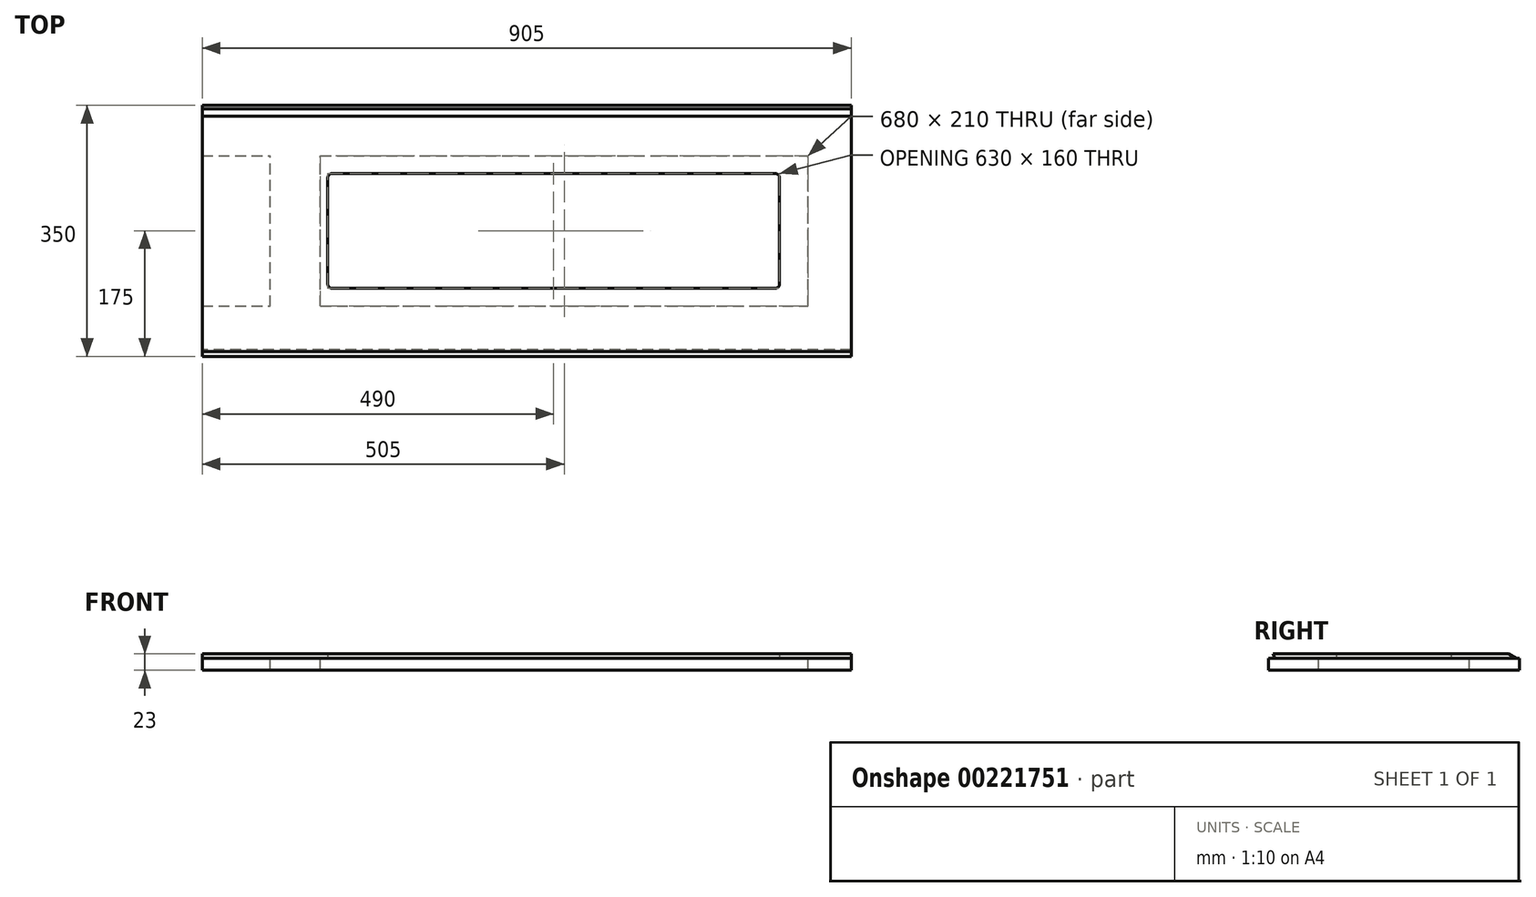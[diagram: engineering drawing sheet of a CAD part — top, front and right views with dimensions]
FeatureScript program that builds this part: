
annotation { "Feature Type Name" : "Feature", "Feature Type Description" : "" }
export const myFeature = defineFeature(function(context is Context, id is Id, definition is map)
    precondition{}
    {
        {
            var Q0;
            Q0=qCreatedBy(makeId("Top.planeOp"),FACE);
            var sketch = newSketch(context, id + "F0", { "sketchPlane" : qUnion([Q0])});
            skLineSegment(sketch, "E0.bottom", {"start": v(-452.5, 175) * mm, "end": v(452.5, 175) * mm});
            skLineSegment(sketch, "E0.top", {"start": v(-452.5, -175) * mm, "end": v(452.5, -175) * mm});
            skLineSegment(sketch, "E0.left", {"start": v(-452.5, 175) * mm, "end": v(-452.5, -175) * mm});
            skLineSegment(sketch, "E0.right", {"start": v(452.5, 175) * mm, "end": v(452.5, -175) * mm});
            skPoint(sketch, "E0.middle", {"position": v(0, 0) * mm});
            skLineSegment(sketch, "E1.bottom", {"start": v(-271.5, 80) * mm, "end": v(346.5, 80) * mm});
            skLineSegment(sketch, "E1.top", {"start": v(-271.5, -80) * mm, "end": v(346.5, -80) * mm});
            skLineSegment(sketch, "E1.left", {"start": v(-277.5, 74) * mm, "end": v(-277.5, -74) * mm});
            skLineSegment(sketch, "E1.right", {"start": v(352.5, 74) * mm, "end": v(352.5, -74) * mm});
            skPoint(sketch, "E2.visualSharp", {"position": v(-277.5, -80) * mm});
            skArc(sketch, "E2.filletArc", {"start": v(-277.5, -74) * mm, "mid": v(-275.74, -78.24) * mm, "end": v(-271.5, -80) * mm});
            skPoint(sketch, "E3.visualSharp", {"position": v(352.5, -80) * mm});
            skArc(sketch, "E3.filletArc", {"start": v(346.5, -80) * mm, "mid": v(350.74, -78.24) * mm, "end": v(352.5, -74) * mm});
            skPoint(sketch, "E4.visualSharp", {"position": v(352.5, 80) * mm});
            skArc(sketch, "E4.filletArc", {"start": v(352.5, 74) * mm, "mid": v(350.74, 78.24) * mm, "end": v(346.5, 80) * mm});
            skLineSegment(sketch, "E5", {"start": v(0, 0) * mm, "end": v(163.88, 0) * mm, "construction": true});
            skLineSegment(sketch, "E6", {"start": v(0, 0) * mm, "end": v(0, -200.2) * mm, "construction": true});
            skPoint(sketch, "E7.visualSharp", {"position": v(-277.5, 80) * mm});
            skArc(sketch, "E7.filletArc", {"start": v(-271.5, 80) * mm, "mid": v(-275.74, 78.24) * mm, "end": v(-277.5, 74) * mm});
            skSolve(sketch);
        }
        {
            var Q0;
            Q0 = qSketchRegion(id + "F0", true);
            extrude(context, id + "F1", {"entities" : qUnion([Q0]), "depth" : 6 * mm});
        }
        {
            var Q0;
            Q0=makeQuery(id+"F1.opExtrude","CAP_FACE",FACE,{"disambiguationData":[OSD([sQuery(id+"F0.wireOp",EDGE,"E0.bottom"),sQuery(id+"F0.wireOp",EDGE,"E0.top"),sQuery(id+"F0.wireOp",EDGE,"E0.left"),sQuery(id+"F0.wireOp",EDGE,"E0.right"),sQuery(id+"F0.wireOp",EDGE,"E1.bottom"),sQuery(id+"F0.wireOp",EDGE,"E1.top"),sQuery(id+"F0.wireOp",EDGE,"E1.left"),sQuery(id+"F0.wireOp",EDGE,"E1.right"),sQuery(id+"F0.wireOp",EDGE,"E2.filletArc"),sQuery(id+"F0.wireOp",EDGE,"E3.filletArc"),sQuery(id+"F0.wireOp",EDGE,"E4.filletArc"),sQuery(id+"F0.wireOp",EDGE,"E7.filletArc")])],"isStart":true});
            var sketch = newSketch(context, id + "F2", { "sketchPlane" : qUnion([Q0])});
            skLineSegment(sketch, "E8.0", {"start": v(-452.5, 175) * mm, "end": v(452.5, 175) * mm});
            skLineSegment(sketch, "E9.0", {"start": v(-452.5, -175) * mm, "end": v(452.5, -175) * mm});
            skLineSegment(sketch, "E10.0", {"start": v(452.5, -175) * mm, "end": v(452.5, 175) * mm});
            skLineSegment(sketch, "E11", {"start": v(-452.5, 105) * mm, "end": v(452.5, 105) * mm});
            skLineSegment(sketch, "E12.0", {"start": v(-452.5, -175) * mm, "end": v(-452.5, 175) * mm});
            skLineSegment(sketch, "E13", {"start": v(-452.5, -105) * mm, "end": v(452.5, -105) * mm});
            skLineSegment(sketch, "E14", {"start": v(392.5, 105) * mm, "end": v(392.5, -105) * mm});
            skLineSegment(sketch, "E15", {"start": v(-287.5, 105) * mm, "end": v(-287.5, -105) * mm});
            skLineSegment(sketch, "E16", {"start": v(-357.5, 105) * mm, "end": v(-357.5, -105) * mm});
            skSolve(sketch);
        }
        {
            var Q0;
            {var subQ5=sQuery(id+"F2.wireOp",EDGE,"E14");Q0=makeQuery(id+"F2.imprint","IMPRINT",FACE,{"disambiguationData":[TD([[makeQuery(id+"F2.imprint","IMPRINT",EDGE,{"derivedFrom":subQ5}),1.0]])]});}
            var Q1;
            {var subQ5=sQuery(id+"F2.wireOp",EDGE,"E8.0");Q1=makeQuery(id+"F2.imprint","IMPRINT",FACE,{"disambiguationData":[TD([[makeQuery(id+"F2.imprint","IMPRINT",EDGE,{"derivedFrom":subQ5}),-1.0]])]});}
            var Q2;
            {var subQ4=sQuery(id+"F2.wireOp",EDGE,"E9.0");Q2=makeQuery(id+"F2.imprint","IMPRINT",FACE,{"disambiguationData":[TD([[makeQuery(id+"F2.imprint","IMPRINT",EDGE,{"derivedFrom":subQ4}),1.0]])]});}
            var Q3;
            {var subQ0=sQuery(id+"F2.wireOp",EDGE,"E15");Q3=makeQuery(id+"F2.imprint","IMPRINT",FACE,{"disambiguationData":[TD([[makeQuery(id+"F2.imprint","IMPRINT",EDGE,{"derivedFrom":subQ0}),-1.0]])]});}
            extrude(context, id + "F3", {"entities" : qUnion([Q0, Q1, Q2, Q3]), "depth" : 17 * mm});
        }
        {
            var Q0;
            Q0=makeQuery(id+"F1.opExtrude","CAP_EDGE",EDGE,{"disambiguationData":[OSD([sQuery(id+"F0.wireOp",EDGE,"E0.bottom")])],"isStart":false});
            chamfer(context, id + "F4", {"entities" : qUnion([Q0]), "chamferType" : ChamferType.OFFSET_ANGLE, "width" : 15 * mm, "oppositeDirection" : true, "angle" : 30 * degree, "tangentPropagation" : true});
        }
        {
            var Q0;
            Q0=makeQuery(id+"F1.opExtrude","CAP_EDGE",EDGE,{"disambiguationData":[OSD([sQuery(id+"F0.wireOp",EDGE,"E0.top")])],"isStart":true});
            chamfer(context, id + "F5", {"entities" : qUnion([Q0]), "chamferType" : ChamferType.OFFSET_ANGLE, "width" : 20 * mm, "oppositeDirection" : false, "angle" : 25 * degree, "tangentPropagation" : true});
        }
    });
